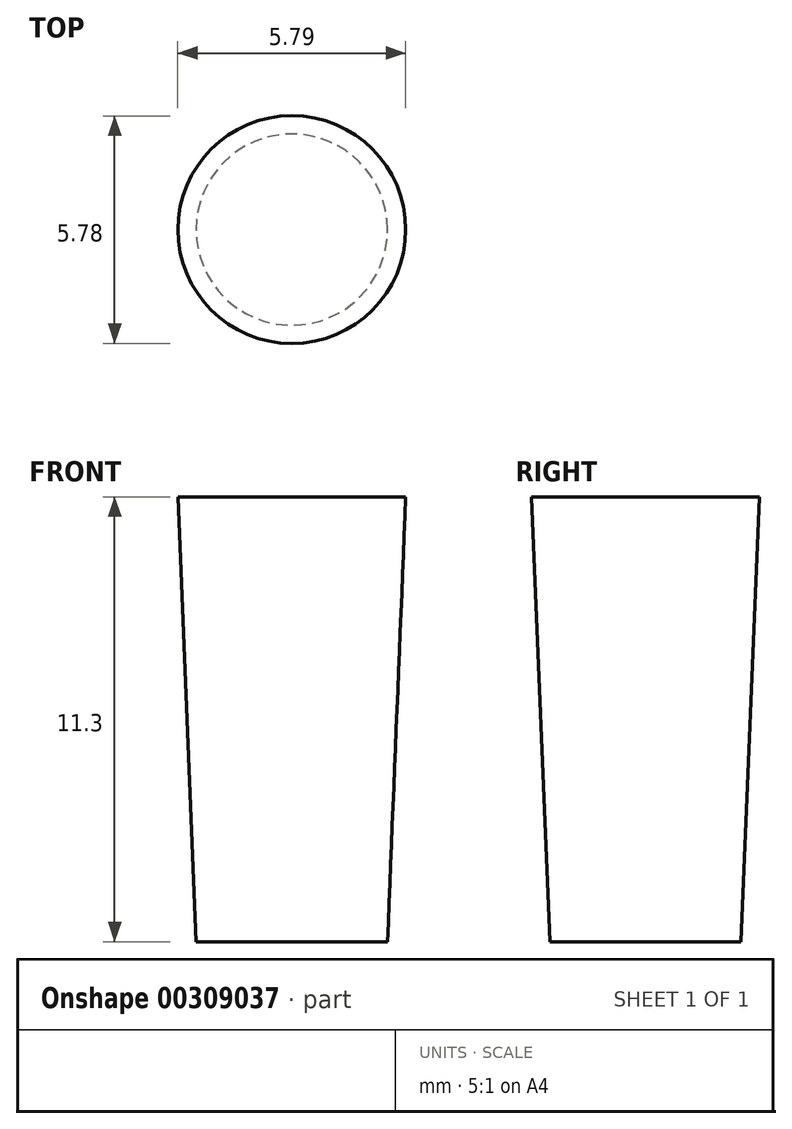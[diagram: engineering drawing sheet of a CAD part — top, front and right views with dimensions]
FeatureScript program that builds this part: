
annotation { "Feature Type Name" : "Feature", "Feature Type Description" : "" }
export const myFeature = defineFeature(function(context is Context, id is Id, definition is map)
    precondition{}
    {
        {
            var Q0;
            Q0=qCreatedBy(makeId("Top.planeOp"),FACE);
            var sketch = newSketch(context, id + "F0", { "sketchPlane" : qUnion([Q0])});
            skCircle(sketch, "E0", {"center": v(-99.28, -10.02) * mm, "radius": 2.43 * mm});
            skSolve(sketch);
        }
        {
            var Q0;
            Q0=makeQuery(id+"F0.imprint","IMPRINT",FACE,{"disambiguationData":[TD([[makeQuery(id+"F0.imprint","IMPRINT",EDGE,{"derivedFrom":sQuery(id+"F0.wireOp",EDGE,"E0")}),1.0]])]});
            extrude(context, id + "F1", {"entities" : qUnion([Q0]), "depth" : 11.3 * mm, "hasDraft" : true, "draftAngle" : 2.35 * degree});
        }
    });
